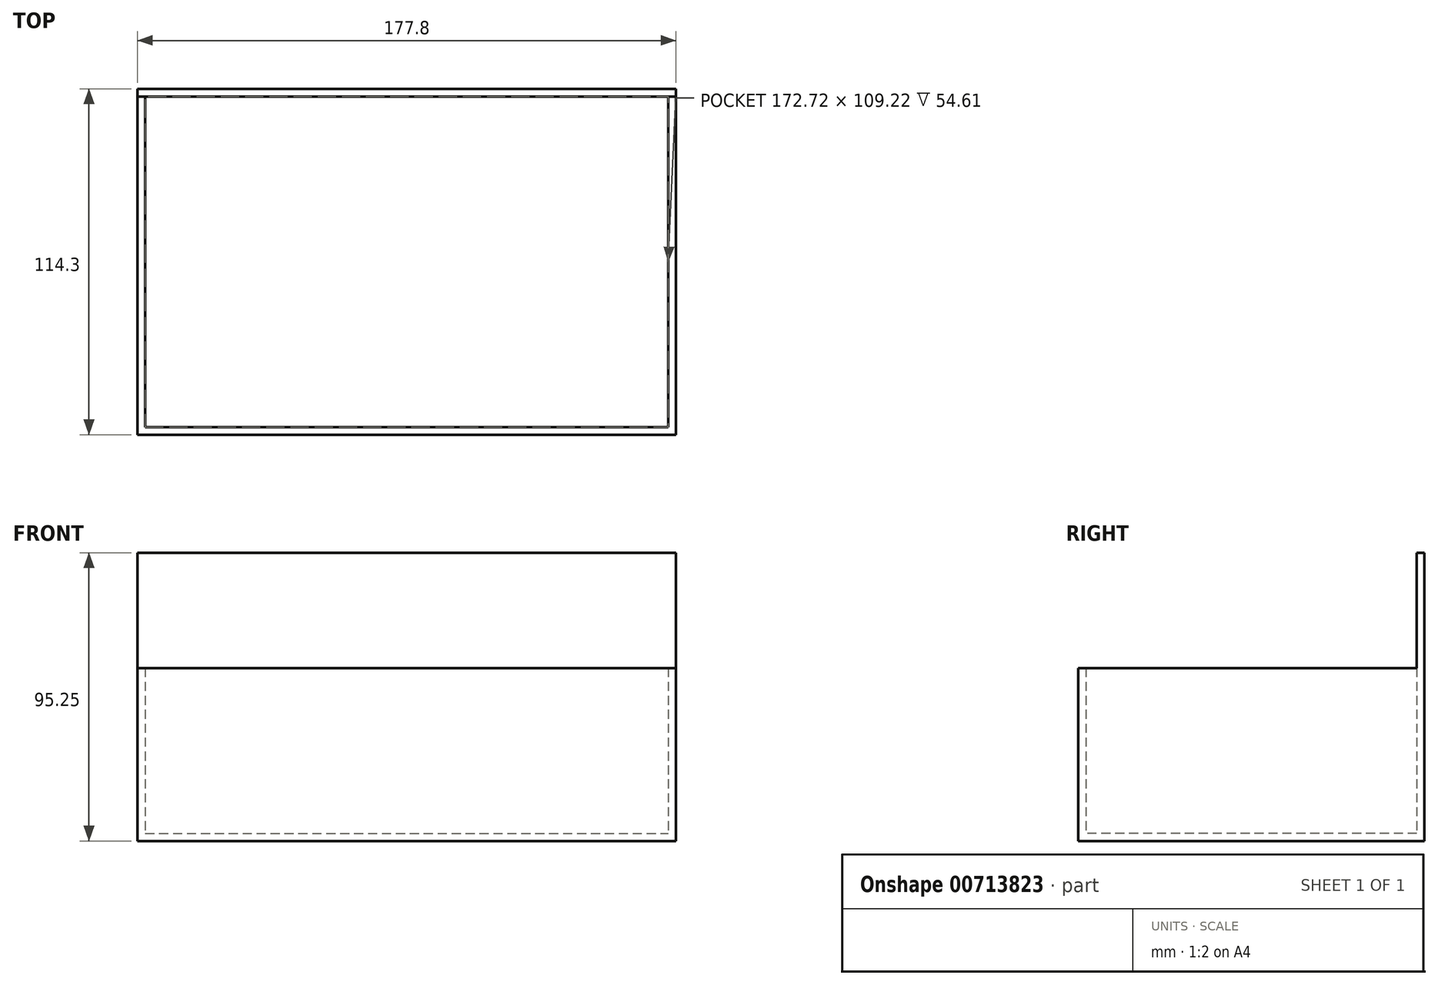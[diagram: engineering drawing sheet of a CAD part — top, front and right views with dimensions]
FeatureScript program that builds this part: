
annotation { "Feature Type Name" : "Feature", "Feature Type Description" : "" }
export const myFeature = defineFeature(function(context is Context, id is Id, definition is map)
    precondition{}
    {
        {
            var Q0;
            Q0=qCreatedBy(makeId("Top.planeOp"),FACE);
            var sketch = newSketch(context, id + "F0", { "sketchPlane" : qUnion([Q0])});
            skLineSegment(sketch, "E0.bottom", {"start": v(-68.21, 78.13) * mm, "end": v(109.59, 78.13) * mm});
            skLineSegment(sketch, "E0.top", {"start": v(-68.21, -36.17) * mm, "end": v(109.59, -36.17) * mm});
            skLineSegment(sketch, "E0.left", {"start": v(-68.21, 78.13) * mm, "end": v(-68.21, -36.17) * mm});
            skLineSegment(sketch, "E0.right", {"start": v(109.59, 78.13) * mm, "end": v(109.59, -36.17) * mm});
            skSolve(sketch);
        }
        {
            var Q0;
            Q0 = qSketchRegion(id + "F0", true);
            extrude(context, id + "F1", {"entities" : qUnion([Q0]), "depth" : 57.15 * mm, "offsetDistance" : 25.4 * mm});
        }
        {
            var Q0;
            Q0=makeQuery(id+"F1.opExtrude","CAP_FACE",FACE,{"disambiguationData":[OSD([sQuery(id+"F0.wireOp",EDGE,"E0.bottom"),sQuery(id+"F0.wireOp",EDGE,"E0.top"),sQuery(id+"F0.wireOp",EDGE,"E0.left"),sQuery(id+"F0.wireOp",EDGE,"E0.right")])],"isStart":false});
            shell(context, id + "F2", {"entities" : qUnion([Q0]), "thickness" : 2.54 * mm});
        }
        {
            var Q0;
            Q0=makeQuery(id+"F1.opExtrude","CAP_FACE",FACE,{"disambiguationData":[OSD([sQuery(id+"F0.wireOp",EDGE,"E0.bottom"),sQuery(id+"F0.wireOp",EDGE,"E0.top"),sQuery(id+"F0.wireOp",EDGE,"E0.left"),sQuery(id+"F0.wireOp",EDGE,"E0.right")])],"isStart":false});
            var sketch = newSketch(context, id + "F3", { "sketchPlane" : qUnion([Q0])});
            skLineSegment(sketch, "E1", {"start": v(-65.67, 75.59) * mm, "end": v(-68.21, 75.59) * mm});
            skLineSegment(sketch, "E2", {"start": v(107.05, 75.59) * mm, "end": v(109.59, 75.59) * mm});
            skSolve(sketch);
        }
        {
            var Q0;
            {var subQ3=sQuery(id+"F3.wireOp",EDGE,"E1");Q0=makeQuery(id+"F3.imprint","IMPRINT",FACE,{"disambiguationData":[TD([[makeQuery(id+"F3.imprint","IMPRINT",EDGE,{"derivedFrom":subQ3}),-1.0]])]});}
            extrude(context, id + "F4", {"entities" : qUnion([Q0]), "operationType" : NewBodyOperationType.ADD, "depth" : 38.1 * mm, "offsetDistance" : 25.4 * mm});
        }
    });
